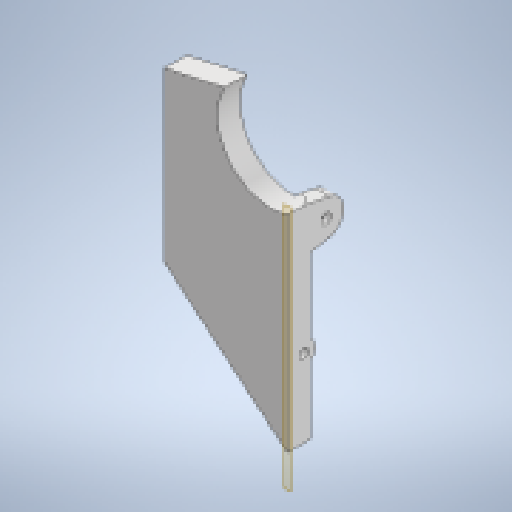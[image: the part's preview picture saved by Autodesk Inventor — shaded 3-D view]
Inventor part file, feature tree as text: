
AUTODESK INVENTOR PART (.ipt)
format: ipt  version: 2023 (Build 270158000, 158)  size: 344,576 bytes
history: native  units: in
note: dims shown in document units (in); Inventor stores cm internally (conversion verified against a paired STEP export)
features: extrude x16, sketch x16, other x13, projected_geometry x10, reference x1
ambient origin geometry x8: Origin, YZ Plane, XZ Plane, XY Plane, X Axis, Y Axis, Z Axis, Center Point
bodies: Body1 (feature_tree)
feature tree (56):
  other  "Bryła1"
  extrude  "Wyciągnięcie proste1"  Depth=0.3436in
  extrude  "Wyciągnięcie proste2"  Depth=0.1969in TaperAngle=0.0deg
  other  "Płaszczyzna konstrukcyjna1"
  extrude  "Wyciągnięcie proste3"  Depth=0.1969in
  extrude  "Wyciągnięcie proste4"  TaperAngle=0.0deg  [1 undecoded]
  extrude  "Wyciągnięcie proste5"  Depth=0.3937in TaperAngle=0.0deg
  sketch  "Szkic6"
  other  "Płaszczyzna konstrukcyjna2"
  extrude  "Wyciągnięcie proste6"  Depth=0.3937in TaperAngle=0.0deg
  extrude  "Wyciągnięcie proste7"  TaperAngle=45.0deg  [1 undecoded]
  extrude  "Wyciągnięcie proste8"  TaperAngle=0.0deg  [1 undecoded]
  extrude  "Wyciągnięcie proste9"  Depth=0.0787in
  extrude  "Wyciągnięcie proste10"  Depth=0.2165in
  extrude  "Wyciągnięcie proste11"  Depth=0.0787in
  extrude  "Wyciągnięcie proste12"  Depth=0.5512in
  extrude  "Wyciągnięcie proste13"  Depth=0.1181in
  extrude  "Wyciągnięcie proste14"  Depth=0.2165in
  other  "Edytuj bezpośrednio1"
  extrude  "Wyciągnięcie proste15"  Depth=0.3937in TaperAngle=0.0deg
  extrude  "Wyciągnięcie proste16"  Depth=0.1181in
  other  "Edytuj bezpośrednio2"
  other  "Edytuj bezpośrednio3"
  sketch  "Szkic1"
  reference  "Odniesienie1"
  sketch  "Szkic2"
  projected_geometry  "Pętla rzutowana1"
  sketch  "Szkic3"
  projected_geometry  "Pętla rzutowana2"
  sketch  "Szkic4"
  projected_geometry  "Pętla rzutowana3"
  sketch  "Szkic5"
  projected_geometry  "Pętla rzutowana4"
  sketch  "Szkic7"
  sketch  "Szkic8"
  projected_geometry  "Pętla rzutowana5"
  sketch  "Szkic9"
  sketch  "Szkic10"
  sketch  "Szkic11"
  projected_geometry  "Pętla rzutowana6"
  sketch  "Szkic12"
  projected_geometry  "Pętla rzutowana7"
  sketch  "Szkic13"
  projected_geometry  "Pętla rzutowana8"
  sketch  "Szkic14"
  projected_geometry  "Pętla rzutowana9"
  sketch  "Szkic15"
  sketch  "Szkic16"
  projected_geometry  "Pętla rzutowana10"
  other  "Zespół2"
  other  "sciana_lewa_v5:1"
  other  "Przesuń1"
  other  "Przesuń2"
  other  "Przesuń3"
  other  "Zespół3"
  other  "minisumopodsr:1"
note: 3 required parameter values undecoded (feature->parameter linkage not recoverable at this tier; creation-order binding heuristic only, values carry confidence <= 0.55)
